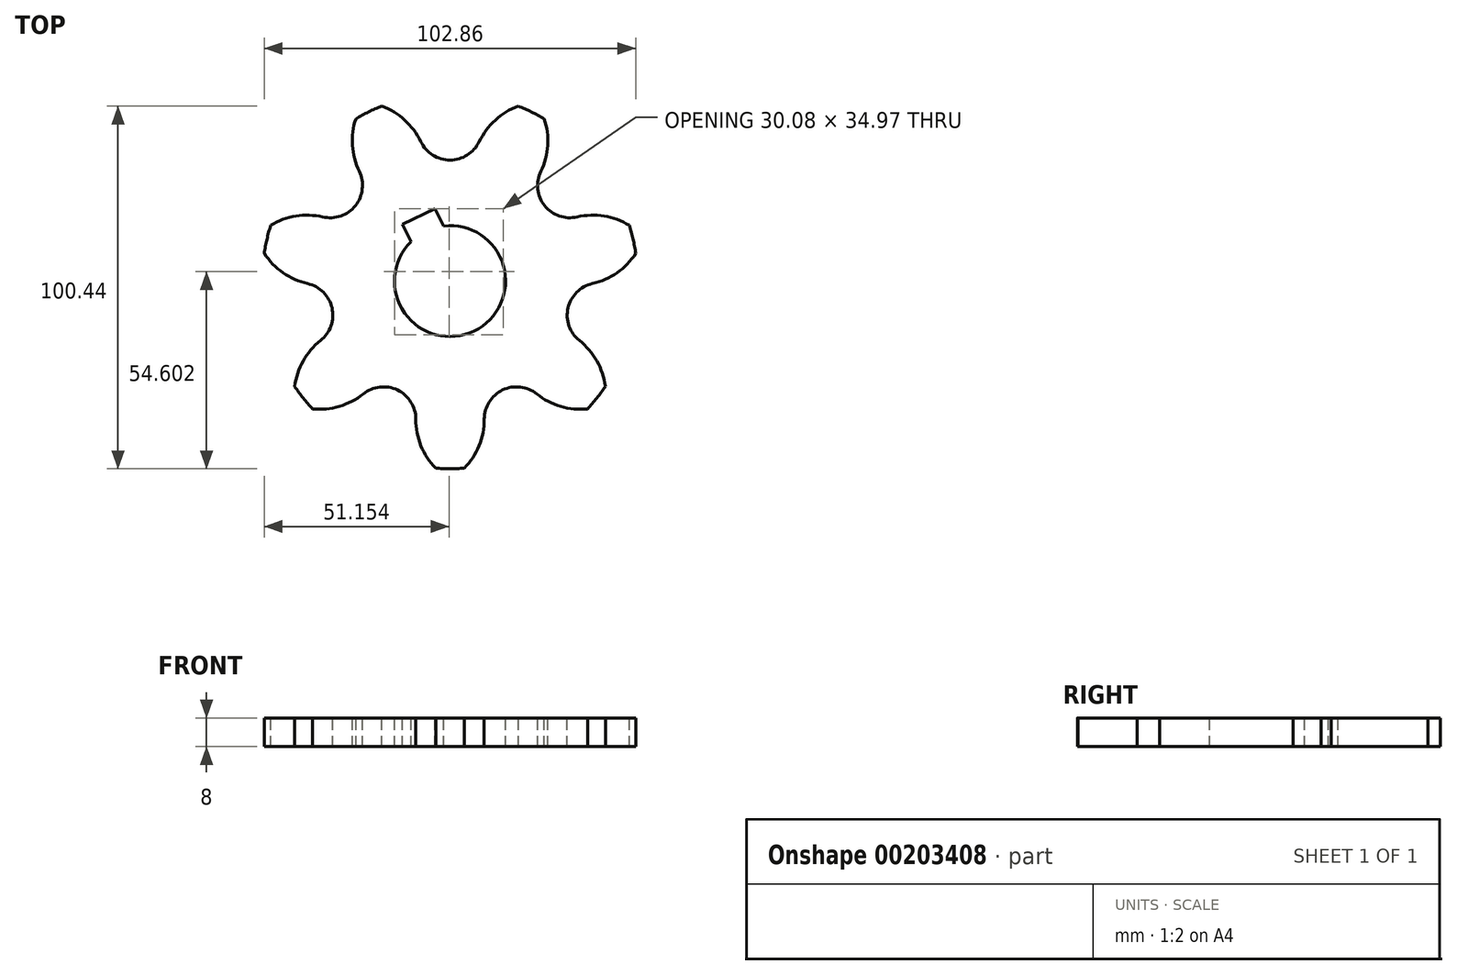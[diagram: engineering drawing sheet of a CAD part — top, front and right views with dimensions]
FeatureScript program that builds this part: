
annotation { "Feature Type Name" : "Feature", "Feature Type Description" : "" }
export const myFeature = defineFeature(function(context is Context, id is Id, definition is map)
    precondition{}
    {
        {
            var Q0;
            Q0=qCreatedBy(makeId("Top.planeOp"),FACE);
            var sketch = newSketch(context, id + "F0", { "sketchPlane" : qUnion([Q0])});
            skLineSegment(sketch, "E0", {"start": v(-13.13, 17.53) * mm, "end": v(-4.12, 21.87) * mm});
            skLineSegment(sketch, "E1", {"start": v(-4.12, 21.87) * mm, "end": v(-1.8, 17.05) * mm});
            skLineSegment(sketch, "E2", {"start": v(-10.81, 12.71) * mm, "end": v(-13.13, 17.53) * mm});
            skArc(sketch, "E3", {"start": v(-10.81, 12.71) * mm, "mid": v(6.67, -12.07) * mm, "end": v(-1.8, 17.05) * mm});
            skArc(sketch, "E4", {"start": v(-0.02, 35.3) * mm, "mid": v(4.77, 36.67) * mm, "end": v(8.09, 40.39) * mm});
            skArc(sketch, "E5", {"start": v(18.91, 50.22) * mm, "mid": v(12.54, 46.36) * mm, "end": v(8.09, 40.39) * mm});
            skArc(sketch, "E6", {"start": v(26.08, 46.77) * mm, "mid": v(22.56, 48.63) * mm, "end": v(18.91, 50.22) * mm});
            skArc(sketch, "E7", {"start": v(25.14, 32.17) * mm, "mid": v(27.03, 39.38) * mm, "end": v(26.08, 46.77) * mm});
            skArc(sketch, "E8", {"start": v(25.14, 32.17) * mm, "mid": v(24.3, 27.26) * mm, "end": v(26.21, 22.66) * mm});
            skArc(sketch, "E9", {"start": v(14.56, -28.4) * mm, "mid": v(10.84, -31.72) * mm, "end": v(9.46, -36.51) * mm});
            skArc(sketch, "E10", {"start": v(3.98, -50.07) * mm, "mid": v(8.04, -43.82) * mm, "end": v(9.46, -36.51) * mm});
            skArc(sketch, "E11", {"start": v(-3.98, -50.07) * mm, "mid": v(0, -50.22) * mm, "end": v(3.98, -50.07) * mm});
            skArc(sketch, "E12", {"start": v(-9.46, -36.51) * mm, "mid": v(-8.04, -43.82) * mm, "end": v(-3.98, -50.07) * mm});
            skArc(sketch, "E13", {"start": v(-9.46, -36.51) * mm, "mid": v(-10.84, -31.72) * mm, "end": v(-14.56, -28.4) * mm});
            skArc(sketch, "E14", {"start": v(-32.67, -5.7) * mm, "mid": v(-35.08, -1.33) * mm, "end": v(-39.44, 1.07) * mm});
            skArc(sketch, "E15", {"start": v(-51.43, 9.44) * mm, "mid": v(-46.25, 4.09) * mm, "end": v(-39.44, 1.07) * mm});
            skArc(sketch, "E16", {"start": v(-49.66, 17.2) * mm, "mid": v(-50.7, 13.35) * mm, "end": v(-51.43, 9.44) * mm});
            skArc(sketch, "E17", {"start": v(-35.23, 19.53) * mm, "mid": v(-42.67, 19.77) * mm, "end": v(-49.66, 17.2) * mm});
            skArc(sketch, "E18", {"start": v(-35.23, 19.53) * mm, "mid": v(-30.25, 19.8) * mm, "end": v(-26.19, 22.69) * mm});
            skArc(sketch, "E19", {"start": v(-14.52, -28.42) * mm, "mid": v(-19.43, -27.59) * mm, "end": v(-24.04, -29.5) * mm});
            skArc(sketch, "E20", {"start": v(-38.06, -33.65) * mm, "mid": v(-30.64, -32.94) * mm, "end": v(-24.04, -29.5) * mm});
            skArc(sketch, "E21", {"start": v(-43.02, -27.44) * mm, "mid": v(-40.66, -30.64) * mm, "end": v(-38.06, -33.65) * mm});
            skArc(sketch, "E22", {"start": v(-35.84, -14.7) * mm, "mid": v(-40.67, -20.36) * mm, "end": v(-43.02, -27.44) * mm});
            skArc(sketch, "E23", {"start": v(-35.84, -14.7) * mm, "mid": v(-32.96, -10.63) * mm, "end": v(-32.67, -5.66) * mm});
            skArc(sketch, "E24", {"start": v(-26.21, 22.66) * mm, "mid": v(-24.3, 27.26) * mm, "end": v(-25.14, 32.17) * mm});
            skArc(sketch, "E25", {"start": v(-26.08, 46.77) * mm, "mid": v(-27.03, 39.38) * mm, "end": v(-25.14, 32.17) * mm});
            skArc(sketch, "E26", {"start": v(-18.91, 50.22) * mm, "mid": v(-22.56, 48.63) * mm, "end": v(-26.08, 46.77) * mm});
            skArc(sketch, "E27", {"start": v(-8.09, 40.39) * mm, "mid": v(-12.54, 46.36) * mm, "end": v(-18.91, 50.22) * mm});
            skArc(sketch, "E28", {"start": v(-8.09, 40.39) * mm, "mid": v(-4.77, 36.67) * mm, "end": v(0.02, 35.3) * mm});
            skArc(sketch, "E29", {"start": v(26.19, 22.69) * mm, "mid": v(30.25, 19.8) * mm, "end": v(35.23, 19.53) * mm});
            skArc(sketch, "E30", {"start": v(49.66, 17.2) * mm, "mid": v(42.67, 19.77) * mm, "end": v(35.23, 19.53) * mm});
            skArc(sketch, "E31", {"start": v(51.43, 9.44) * mm, "mid": v(50.7, 13.35) * mm, "end": v(49.66, 17.2) * mm});
            skArc(sketch, "E32", {"start": v(39.44, 1.07) * mm, "mid": v(46.25, 4.09) * mm, "end": v(51.43, 9.44) * mm});
            skArc(sketch, "E33", {"start": v(39.44, 1.07) * mm, "mid": v(35.08, -1.33) * mm, "end": v(32.67, -5.7) * mm});
            skArc(sketch, "E34", {"start": v(32.67, -5.66) * mm, "mid": v(32.96, -10.63) * mm, "end": v(35.84, -14.7) * mm});
            skArc(sketch, "E35", {"start": v(43.02, -27.44) * mm, "mid": v(40.67, -20.36) * mm, "end": v(35.84, -14.7) * mm});
            skArc(sketch, "E36", {"start": v(38.06, -33.65) * mm, "mid": v(40.66, -30.64) * mm, "end": v(43.02, -27.44) * mm});
            skArc(sketch, "E37", {"start": v(24.04, -29.5) * mm, "mid": v(30.64, -32.94) * mm, "end": v(38.06, -33.65) * mm});
            skArc(sketch, "E38", {"start": v(24.04, -29.5) * mm, "mid": v(19.43, -27.59) * mm, "end": v(14.52, -28.42) * mm});
            skSolve(sketch);
        }
        {
            var Q0;
            Q0=makeQuery(id+"F0.imprint","IMPRINT",FACE,{"disambiguationData":[TD([[makeQuery(id+"F0.imprint","IMPRINT",EDGE,{"derivedFrom":sQuery(id+"F0.wireOp",EDGE,"E0")}),1.0]])]});
            extrude(context, id + "F1", {"entities" : qUnion([Q0]), "oppositeDirection" : true, "depth" : 8 * mm});
        }
    });
